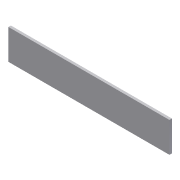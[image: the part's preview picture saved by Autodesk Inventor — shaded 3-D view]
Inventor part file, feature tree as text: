
AUTODESK INVENTOR PART (.ipt)
format: ipt  version: 2012 (Build 160160000, 160)  size: 62,464 bytes
history: native  units: in
note: dims shown in document units (in); Inventor stores cm internally (conversion verified against a paired STEP export)
features: extrude x1, plane x1, sketch x1
ambient origin geometry x8: Origin, YZ Plane, XZ Plane, XY Plane, X Axis, Y Axis, Z Axis, Center Point
bodies: Solid1 (feature_tree)
feature tree (3):
  extrude  "Extrusion1"  Depth=3.0in
  plane  "Work Plane2"
  sketch  "Sketch1"  dims[d0=16.0in d1=3.0in d2=0.25in d3=0.0in d5=-1.5in]
